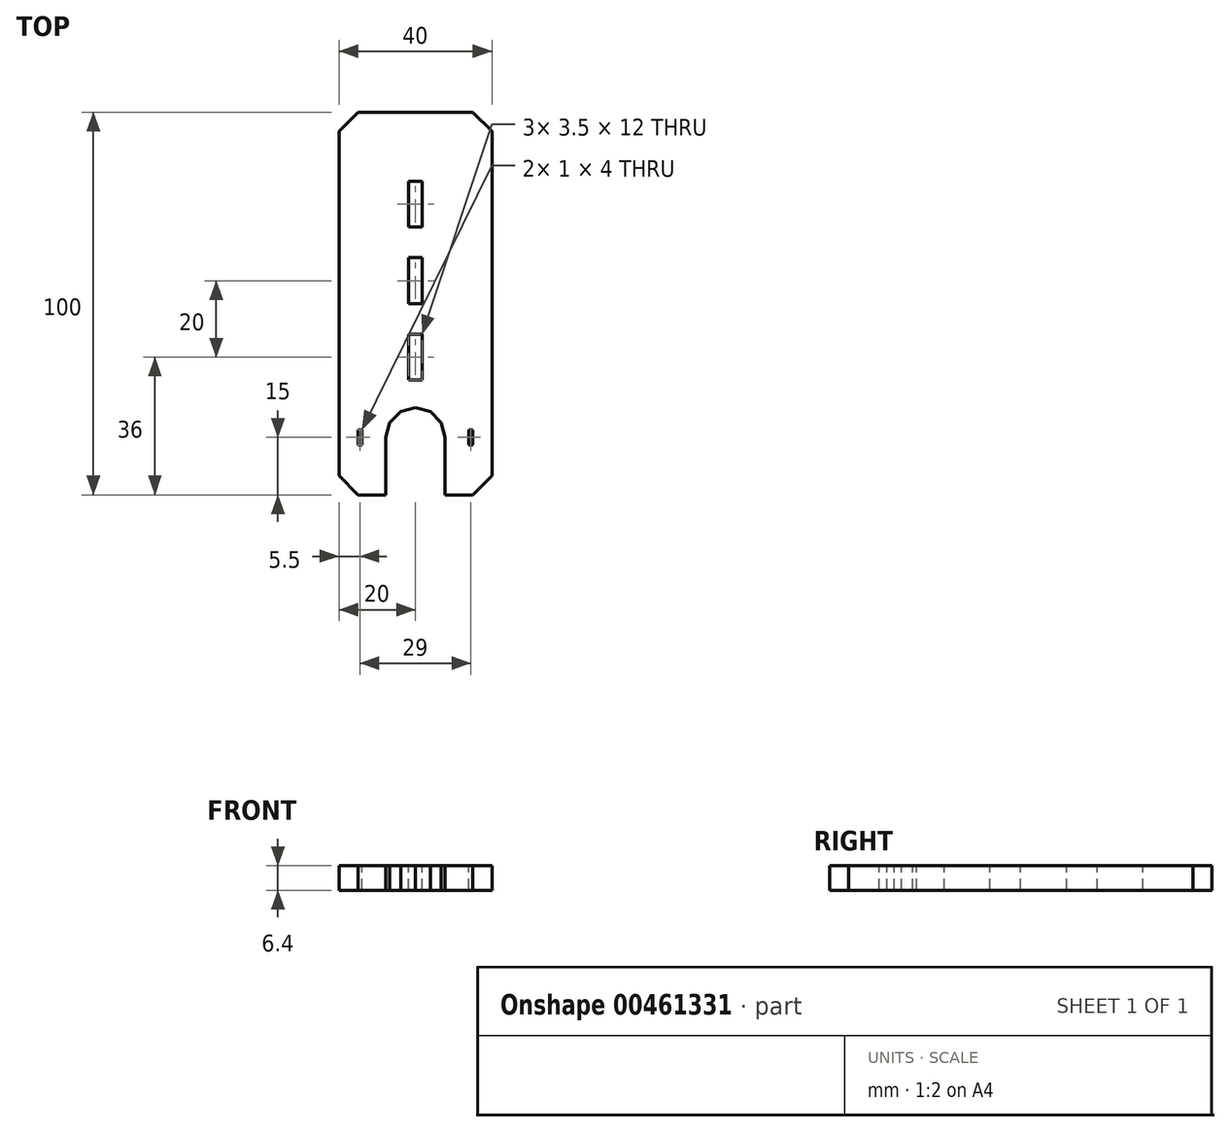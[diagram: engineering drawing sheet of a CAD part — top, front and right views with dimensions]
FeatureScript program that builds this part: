
annotation { "Feature Type Name" : "Feature", "Feature Type Description" : "" }
export const myFeature = defineFeature(function(context is Context, id is Id, definition is map)
    precondition{}
    {
        {
            var Q0;
            Q0=qCreatedBy(makeId("Top.planeOp"),FACE);
            var sketch = newSketch(context, id + "F0", { "sketchPlane" : qUnion([Q0])});
            skLineSegment(sketch, "E0.bottom", {"start": v(20, -50) * mm, "end": v(-20, -50) * mm});
            skLineSegment(sketch, "E0.top", {"start": v(20, 50) * mm, "end": v(-20, 50) * mm});
            skLineSegment(sketch, "E0.left", {"start": v(20, -50) * mm, "end": v(20, 50) * mm});
            skLineSegment(sketch, "E0.right", {"start": v(-20, -50) * mm, "end": v(-20, 50) * mm});
            skPoint(sketch, "E0.middle", {"position": v(0, 0) * mm});
            skSolve(sketch);
        }
        {
            var Q0;
            Q0 = qSketchRegion(id + "F0", true);
            extrude(context, id + "F1", {"entities" : qUnion([Q0]), "depth" : 6.4 * mm});
        }
        {
            var Q0;
            Q0=makeQuery(id+"F1.opExtrude","SWEPT_EDGE",EDGE,{"disambiguationData":[OSD([sQuery(id+"F0.wireOp",EDGE,"E0.bottom"),sQuery(id+"F0.wireOp",EDGE,"E0.right")])]});
            var Q1;
            Q1=makeQuery(id+"F1.opExtrude","SWEPT_EDGE",EDGE,{"disambiguationData":[OSD([sQuery(id+"F0.wireOp",EDGE,"E0.bottom"),sQuery(id+"F0.wireOp",EDGE,"E0.left")])]});
            var Q2;
            Q2=makeQuery(id+"F1.opExtrude","SWEPT_EDGE",EDGE,{"disambiguationData":[OSD([sQuery(id+"F0.wireOp",EDGE,"E0.top"),sQuery(id+"F0.wireOp",EDGE,"E0.left")])]});
            var Q3;
            Q3=makeQuery(id+"F1.opExtrude","SWEPT_EDGE",EDGE,{"disambiguationData":[OSD([sQuery(id+"F0.wireOp",EDGE,"E0.top"),sQuery(id+"F0.wireOp",EDGE,"E0.right")])]});
            chamfer(context, id + "F2", {"entities" : qUnion([Q0, Q1, Q2, Q3]), "width" : 5 * mm, "tangentPropagation" : true});
        }
        {
            var Q0;
            Q0=makeQuery(id+"F1.opExtrude","CAP_FACE",FACE,{"disambiguationData":[OSD([sQuery(id+"F0.wireOp",EDGE,"E0.bottom"),sQuery(id+"F0.wireOp",EDGE,"E0.top"),sQuery(id+"F0.wireOp",EDGE,"E0.left"),sQuery(id+"F0.wireOp",EDGE,"E0.right")])],"isStart":false});
            var sketch = newSketch(context, id + "F3", { "sketchPlane" : qUnion([Q0])});
            skCircle(sketch, "E1.cCircle", {"center": v(0, -35) * mm, "radius": 7.5 * mm, "construction": true});
            skLineSegment(sketch, "E1.0", {"start": v(6.72, -38.88) * mm, "end": v(3.88, -41.72) * mm});
            skLineSegment(sketch, "E1.1", {"start": v(3.88, -41.72) * mm, "end": v(0, -42.76) * mm});
            skLineSegment(sketch, "E1.2", {"start": v(0, -42.76) * mm, "end": v(-3.88, -41.72) * mm});
            skLineSegment(sketch, "E1.3", {"start": v(-3.88, -41.72) * mm, "end": v(-6.72, -38.88) * mm});
            skLineSegment(sketch, "E1.4", {"start": v(-6.72, -38.88) * mm, "end": v(-7.76, -35) * mm});
            skLineSegment(sketch, "E1.5", {"start": v(-7.76, -35) * mm, "end": v(-6.72, -31.12) * mm});
            skLineSegment(sketch, "E1.6", {"start": v(-6.72, -31.12) * mm, "end": v(-3.88, -28.28) * mm});
            skLineSegment(sketch, "E1.7", {"start": v(-3.88, -28.28) * mm, "end": v(0, -27.24) * mm});
            skLineSegment(sketch, "E1.8", {"start": v(0, -27.24) * mm, "end": v(3.88, -28.28) * mm});
            skLineSegment(sketch, "E1.9", {"start": v(3.88, -28.28) * mm, "end": v(6.72, -31.12) * mm});
            skLineSegment(sketch, "E1.10", {"start": v(6.72, -31.12) * mm, "end": v(7.76, -35) * mm});
            skLineSegment(sketch, "E1.11", {"start": v(7.76, -35) * mm, "end": v(6.72, -38.88) * mm});
            skPoint(sketch, "E1.0.midPoint", {"position": v(5.3, -40.3) * mm});
            skLineSegment(sketch, "E2", {"start": v(-7.76, -35) * mm, "end": v(-7.76, -50) * mm});
            skLineSegment(sketch, "E3", {"start": v(7.76, -35) * mm, "end": v(7.76, -50) * mm});
            skSolve(sketch);
        }
        {
            var Q0;
            Q0=makeQuery(id+"F3.imprint","IMPRINT",FACE,{"disambiguationData":[TD([[makeQuery(id+"F3.imprint","IMPRINT",EDGE,{"derivedFrom":sQuery(id+"F3.wireOp",EDGE,"E1.0")}),-1.0]])]});
            var Q1;
            Q1=makeQuery(id+"F3.imprint","IMPRINT",FACE,{"disambiguationData":[TD([[makeQuery(id+"F3.imprint","IMPRINT",EDGE,{"derivedFrom":sQuery(id+"F3.wireOp",EDGE,"E1.0")}),1.0]])]});
            extrude(context, id + "F4", {"entities" : qUnion([Q0, Q1]), "operationType" : NewBodyOperationType.REMOVE, "endBound" : BoundingType.THROUGH_ALL, "oppositeDirection" : true, "depth" : 25 * mm});
        }
        {
            var Q0;
            Q0=makeQuery(id+"F1.opExtrude","CAP_FACE",FACE,{"disambiguationData":[OSD([sQuery(id+"F0.wireOp",EDGE,"E0.bottom"),sQuery(id+"F0.wireOp",EDGE,"E0.top"),sQuery(id+"F0.wireOp",EDGE,"E0.left"),sQuery(id+"F0.wireOp",EDGE,"E0.right")])],"isStart":false});
            var sketch = newSketch(context, id + "F5", { "sketchPlane" : qUnion([Q0])});
            skLineSegment(sketch, "E4.bottom", {"start": v(15, -37) * mm, "end": v(14, -37) * mm});
            skLineSegment(sketch, "E4.top", {"start": v(15, -33) * mm, "end": v(14, -33) * mm});
            skLineSegment(sketch, "E4.left", {"start": v(15, -37) * mm, "end": v(15, -33) * mm});
            skLineSegment(sketch, "E4.right", {"start": v(14, -37) * mm, "end": v(14, -33) * mm});
            skPoint(sketch, "E4.middle", {"position": v(14.5, -35) * mm});
            skLineSegment(sketch, "E5.MirrorCS", {"start": v(-15, -37) * mm, "end": v(-14, -37) * mm});
            skLineSegment(sketch, "E6.MirrorCS", {"start": v(-15, -33) * mm, "end": v(-14, -33) * mm});
            skPoint(sketch, "E7.MirrorP", {"position": v(-14.5, -35) * mm});
            skLineSegment(sketch, "E8.MirrorCS", {"start": v(-14, -37) * mm, "end": v(-14, -33) * mm});
            skLineSegment(sketch, "E9.MirrorCS", {"start": v(-15, -37) * mm, "end": v(-15, -33) * mm});
            skSolve(sketch);
        }
        {
            var Q0;
            Q0 = qSketchRegion(id + "F5", true);
            extrude(context, id + "F6", {"entities" : qUnion([Q0]), "operationType" : NewBodyOperationType.REMOVE, "endBound" : BoundingType.THROUGH_ALL, "oppositeDirection" : true, "depth" : 25 * mm});
        }
        {
            var Q0;
            Q0=makeQuery(id+"F3.imprint","IMPRINT",FACE,{"disambiguationData":[TD([[makeQuery(id+"F3.imprint","IMPRINT",EDGE,{"derivedFrom":sQuery(id+"F3.wireOp",EDGE,"E1.5")}),1.0]])]});
            var sketch = newSketch(context, id + "F7", { "sketchPlane" : qUnion([Q0])});
            skLineSegment(sketch, "E10.bottom", {"start": v(1.75, 0) * mm, "end": v(-1.75, 0) * mm});
            skLineSegment(sketch, "E10.top", {"start": v(1.75, 12) * mm, "end": v(-1.75, 12) * mm});
            skLineSegment(sketch, "E10.left", {"start": v(1.75, 0) * mm, "end": v(1.75, 12) * mm});
            skLineSegment(sketch, "E10.right", {"start": v(-1.75, 0) * mm, "end": v(-1.75, 12) * mm});
            skPoint(sketch, "E10.middle", {"position": v(0, 6) * mm});
            skLineSegment(sketch, "E11.bottom", {"start": v(1.75, -20) * mm, "end": v(-1.75, -20) * mm});
            skLineSegment(sketch, "E11.top", {"start": v(1.75, -8) * mm, "end": v(-1.75, -8) * mm});
            skLineSegment(sketch, "E11.left", {"start": v(1.75, -20) * mm, "end": v(1.75, -8) * mm});
            skLineSegment(sketch, "E11.right", {"start": v(-1.75, -20) * mm, "end": v(-1.75, -8) * mm});
            skPoint(sketch, "E11.middle", {"position": v(0, -14) * mm});
            skLineSegment(sketch, "E12.bottom", {"start": v(1.75, 20) * mm, "end": v(-1.75, 20) * mm});
            skLineSegment(sketch, "E12.top", {"start": v(1.75, 32) * mm, "end": v(-1.75, 32) * mm});
            skLineSegment(sketch, "E12.left", {"start": v(1.75, 20) * mm, "end": v(1.75, 32) * mm});
            skLineSegment(sketch, "E12.right", {"start": v(-1.75, 20) * mm, "end": v(-1.75, 32) * mm});
            skPoint(sketch, "E12.middle", {"position": v(0, 26) * mm});
            skSolve(sketch);
        }
        {
            var Q0;
            Q0 = qSketchRegion(id + "F7", true);
            extrude(context, id + "F8", {"entities" : qUnion([Q0]), "operationType" : NewBodyOperationType.REMOVE, "endBound" : BoundingType.THROUGH_ALL, "oppositeDirection" : true, "depth" : 25 * mm});
        }
    });
